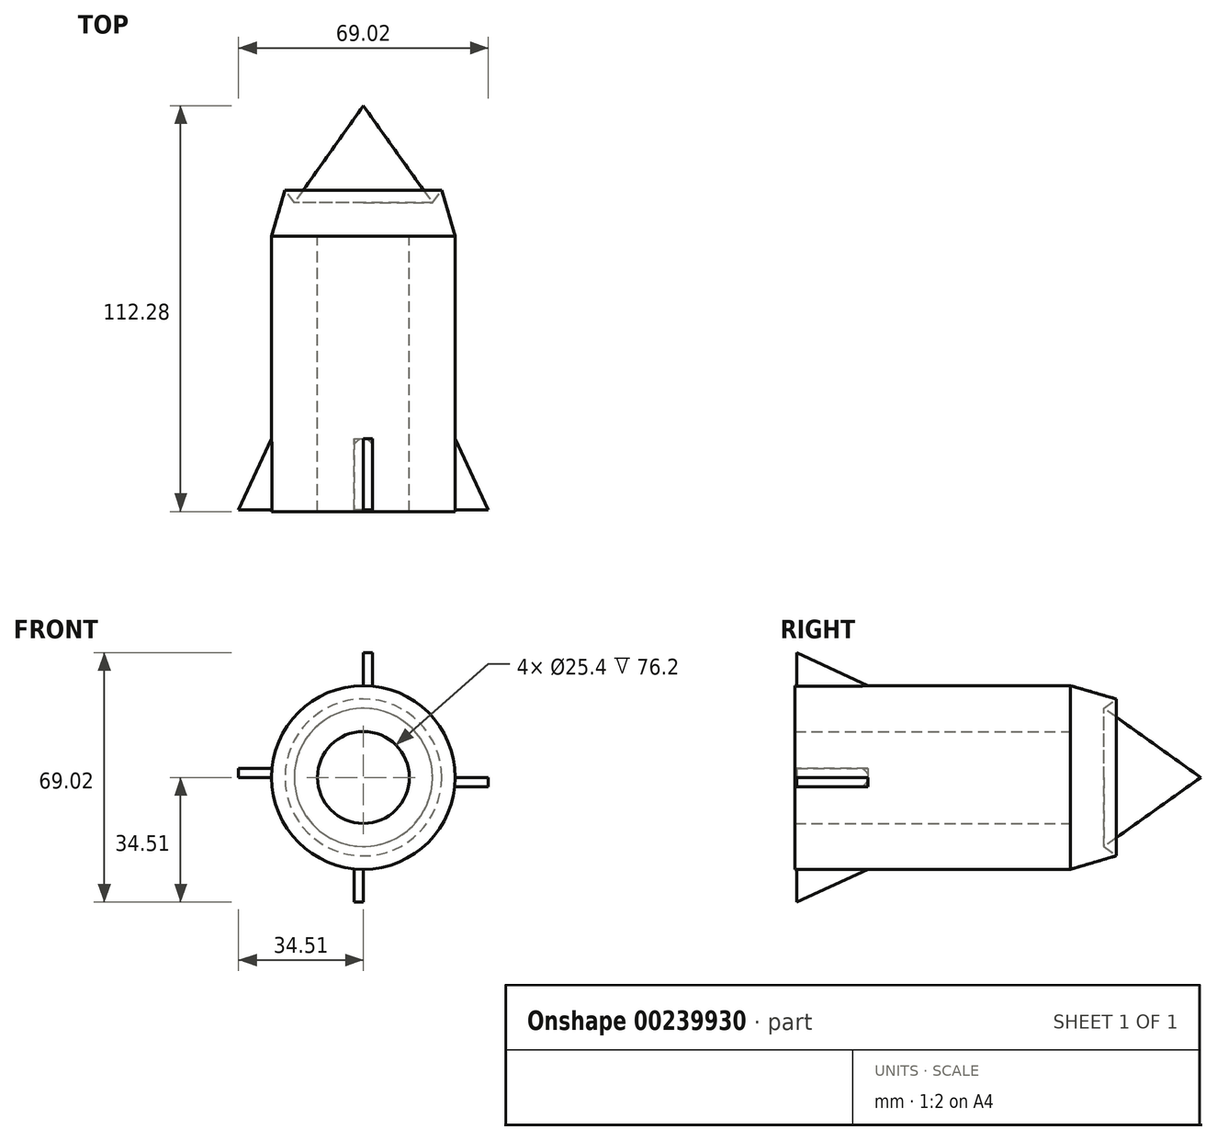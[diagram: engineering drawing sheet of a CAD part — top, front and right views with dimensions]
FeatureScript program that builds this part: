
annotation { "Feature Type Name" : "Feature", "Feature Type Description" : "" }
export const myFeature = defineFeature(function(context is Context, id is Id, definition is map)
    precondition{}
    {
        {
            var Q0;
            Q0=qCreatedBy(makeId("Front.planeOp"),FACE);
            var sketch = newSketch(context, id + "F0", { "sketchPlane" : qUnion([Q0])});
            skCircle(sketch, "E0", {"center": v(0, 0) * mm, "radius": 25.4 * mm});
            skCircle(sketch, "E1", {"center": v(0, 0) * mm, "radius": 12.7 * mm});
            skSolve(sketch);
        }
        {
            var Q0;
            Q0 = qSketchRegion(id + "F0", true);
            extrude(context, id + "F1", {"entities" : qUnion([Q0]), "depth" : 76.2 * mm});
        }
        {
            var Q0;
            Q0=qCreatedBy(makeId("Top.planeOp"),FACE);
            var sketch = newSketch(context, id + "F2", { "sketchPlane" : qUnion([Q0])});
            skLineSegment(sketch, "E2", {"start": v(-25.39, 0) * mm, "end": v(-21.68, 12.7) * mm});
            skLineSegment(sketch, "E3", {"start": v(-21.68, 12.7) * mm, "end": v(-19.11, 9.27) * mm});
            skLineSegment(sketch, "E4", {"start": v(-19.11, 9.27) * mm, "end": v(0, 36.08) * mm});
            skLineSegment(sketch, "E5", {"start": v(0, 36.08) * mm, "end": v(0, 0) * mm});
            skLineSegment(sketch, "E6", {"start": v(0, 0) * mm, "end": v(-25.39, 0) * mm});
            skSolve(sketch);
        }
        {
            var Q0;
            Q0 = qSketchRegion(id + "F2", true);
            var Q1;
            Q1=sQuery(id+"F2.wireOp",EDGE,"E5");
            revolve(context, id + "F3", {"operationType" : NewBodyOperationType.ADD, "entities" : qUnion([Q0]), "axis" : qUnion([Q1]), "revolveType" : RevolveType.FULL});
        }
        {
            var Q0;
            Q0=qCreatedBy(makeId("Top.planeOp"),FACE);
            var sketch = newSketch(context, id + "F4", { "sketchPlane" : qUnion([Q0])});
            skLineSegment(sketch, "E7", {"start": v(-25.39, -56.05) * mm, "end": v(-34.51, -75.73) * mm});
            skLineSegment(sketch, "E8", {"start": v(-34.51, -75.73) * mm, "end": v(-23.96, -75.73) * mm});
            skLineSegment(sketch, "E9", {"start": v(-23.96, -75.73) * mm, "end": v(-25.39, -56.05) * mm});
            skSolve(sketch);
        }
        {
            var Q0;
            Q0 = qSketchRegion(id + "F4", true);
            extrude(context, id + "F5", {"entities" : qUnion([Q0]), "operationType" : NewBodyOperationType.ADD, "depth" : 2.54 * mm});
        }
        {
            var Q0;
            Q0=makeQuery(id+"F1.opExtrude","SWEPT_BODY",BODY,{"disambiguationData":[OSD([sQuery(id+"F0.wireOp",EDGE,"E0"),sQuery(id+"F0.wireOp",EDGE,"E1")])]});
            var Q1;
            Q1=makeQuery(id+"F1.opExtrude","SWEPT_FACE",FACE,{"disambiguationData":[OSD([sQuery(id+"F0.wireOp",EDGE,"E1")])]});
            circularPattern(context, id + "F6", {"entities" : qUnion([Q0]), "axis" : qUnion([Q1]), "angle" : 360 * degree, "instanceCount" : 4, "equalSpace" : true});
        }
    });
